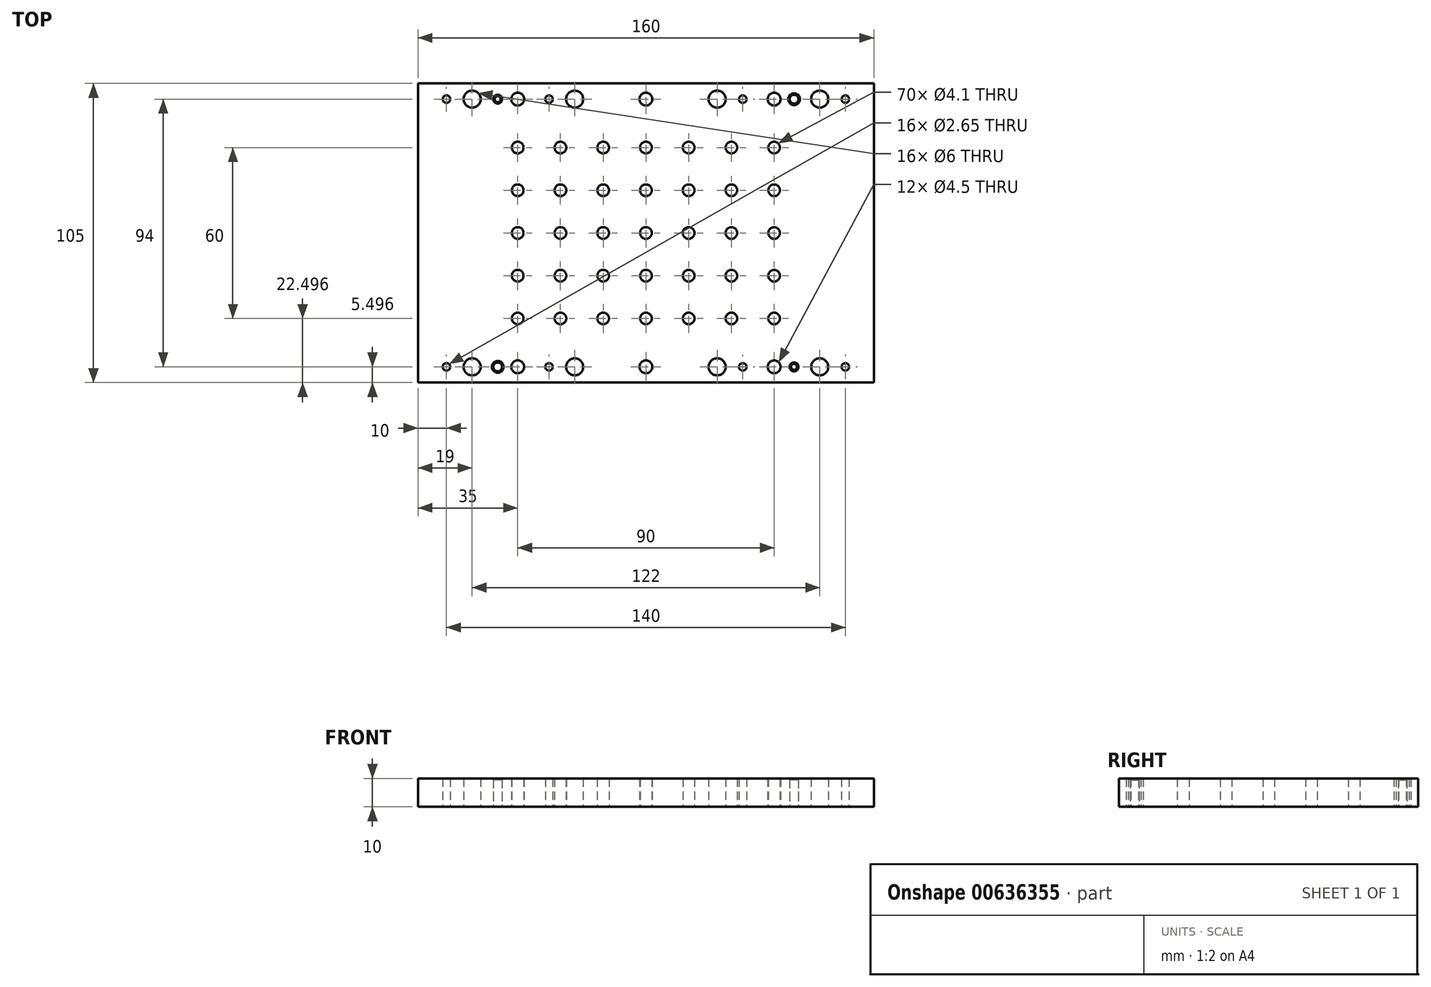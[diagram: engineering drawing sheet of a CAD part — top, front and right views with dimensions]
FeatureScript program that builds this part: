
annotation { "Feature Type Name" : "Feature", "Feature Type Description" : "" }
export const myFeature = defineFeature(function(context is Context, id is Id, definition is map)
    precondition{}
    {
        {
            var Q0;
            Q0=qCreatedBy(makeId("Top.planeOp"),FACE);
            var sketch = newSketch(context, id + "F0", { "sketchPlane" : qUnion([Q0])});
            skLineSegment(sketch, "E0.bottom", {"start": v(-90.54, 47.28) * mm, "end": v(69.46, 47.28) * mm});
            skLineSegment(sketch, "E0.top", {"start": v(-90.54, -57.72) * mm, "end": v(69.46, -57.72) * mm});
            skLineSegment(sketch, "E0.right", {"start": v(69.46, 47.28) * mm, "end": v(69.46, -57.72) * mm});
            skLineSegment(sketch, "E1", {"start": v(-90.54, -5.22) * mm, "end": v(69.46, -5.22) * mm, "construction": true});
            skCircle(sketch, "E2", {"center": v(-80.54, 41.78) * mm, "radius": 1.32 * mm});
            skCircle(sketch, "E3", {"center": v(-62.54, 41.78) * mm, "radius": 1.55 * mm});
            skCircle(sketch, "E4", {"center": v(-71.54, 41.78) * mm, "radius": 3 * mm});
            skCircle(sketch, "E5", {"center": v(-55.54, 41.78) * mm, "radius": 2.25 * mm});
            skCircle(sketch, "E6", {"center": v(-10.54, 41.78) * mm, "radius": 2.25 * mm});
            skCircle(sketch, "E7", {"center": v(-44.54, 41.78) * mm, "radius": 1.32 * mm});
            skCircle(sketch, "E8", {"center": v(-35.54, 41.78) * mm, "radius": 3 * mm});
            skCircle(sketch, "E9.MirrorC", {"center": v(50.46, 41.78) * mm, "radius": 3 * mm});
            skCircle(sketch, "E10.MirrorC", {"center": v(34.46, 41.78) * mm, "radius": 2.25 * mm});
            skCircle(sketch, "E11.MirrorC", {"center": v(14.46, 41.78) * mm, "radius": 3 * mm});
            skCircle(sketch, "E12.MirrorC", {"center": v(59.46, 41.78) * mm, "radius": 1.32 * mm});
            skCircle(sketch, "E13.MirrorC", {"center": v(41.46, 41.78) * mm, "radius": 1.55 * mm});
            skCircle(sketch, "E14.MirrorC", {"center": v(23.46, 41.78) * mm, "radius": 1.32 * mm});
            skCircle(sketch, "E15.MirrorC", {"center": v(59.46, -52.22) * mm, "radius": 1.32 * mm});
            skCircle(sketch, "E16.MirrorC", {"center": v(50.46, -52.22) * mm, "radius": 3 * mm});
            skCircle(sketch, "E17.MirrorC", {"center": v(41.46, -52.22) * mm, "radius": 1.55 * mm});
            skCircle(sketch, "E18.MirrorC", {"center": v(34.46, -52.22) * mm, "radius": 2.25 * mm});
            skCircle(sketch, "E19.MirrorC", {"center": v(23.46, -52.22) * mm, "radius": 1.32 * mm});
            skCircle(sketch, "E20.MirrorC", {"center": v(14.46, -52.22) * mm, "radius": 3 * mm});
            skCircle(sketch, "E21.MirrorC", {"center": v(-10.54, -52.22) * mm, "radius": 2.25 * mm});
            skCircle(sketch, "E22.MirrorC", {"center": v(-35.54, -52.22) * mm, "radius": 3 * mm});
            skCircle(sketch, "E23.MirrorC", {"center": v(-44.54, -52.22) * mm, "radius": 1.32 * mm});
            skCircle(sketch, "E24.MirrorC", {"center": v(-55.54, -52.22) * mm, "radius": 2.25 * mm});
            skCircle(sketch, "E25.MirrorC", {"center": v(-62.54, -52.22) * mm, "radius": 1.55 * mm});
            skCircle(sketch, "E26.MirrorC", {"center": v(-71.54, -52.22) * mm, "radius": 3 * mm});
            skCircle(sketch, "E27.MirrorC", {"center": v(-80.54, -52.22) * mm, "radius": 1.32 * mm});
            skLineSegment(sketch, "E28", {"start": v(-90.54, 47.28) * mm, "end": v(-90.54, -57.72) * mm});
            skCircle(sketch, "E29", {"center": v(-55.54, -35.22) * mm, "radius": 2.05 * mm});
            skCircle(sketch, "E30.0.1.0", {"center": v(-55.54, -20.22) * mm, "radius": 2.05 * mm});
            skCircle(sketch, "E30.0.2.0", {"center": v(-55.54, -5.22) * mm, "radius": 2.05 * mm});
            skCircle(sketch, "E30.0.3.0", {"center": v(-55.54, 9.78) * mm, "radius": 2.05 * mm});
            skCircle(sketch, "E30.0.4.0", {"center": v(-55.54, 24.78) * mm, "radius": 2.05 * mm});
            skCircle(sketch, "E30.1.0.0", {"center": v(-40.54, -35.22) * mm, "radius": 2.05 * mm});
            skCircle(sketch, "E30.1.1.0", {"center": v(-40.54, -20.22) * mm, "radius": 2.05 * mm});
            skCircle(sketch, "E30.1.2.0", {"center": v(-40.54, -5.22) * mm, "radius": 2.05 * mm});
            skCircle(sketch, "E30.1.3.0", {"center": v(-40.54, 9.78) * mm, "radius": 2.05 * mm});
            skCircle(sketch, "E30.1.4.0", {"center": v(-40.54, 24.78) * mm, "radius": 2.05 * mm});
            skCircle(sketch, "E30.2.0.0", {"center": v(-25.54, -35.22) * mm, "radius": 2.05 * mm});
            skCircle(sketch, "E30.2.1.0", {"center": v(-25.54, -20.22) * mm, "radius": 2.05 * mm});
            skCircle(sketch, "E30.2.2.0", {"center": v(-25.54, -5.22) * mm, "radius": 2.05 * mm});
            skCircle(sketch, "E30.2.3.0", {"center": v(-25.54, 9.78) * mm, "radius": 2.05 * mm});
            skCircle(sketch, "E30.2.4.0", {"center": v(-25.54, 24.78) * mm, "radius": 2.05 * mm});
            skCircle(sketch, "E30.3.0.0", {"center": v(-10.54, -35.22) * mm, "radius": 2.05 * mm});
            skCircle(sketch, "E30.3.1.0", {"center": v(-10.54, -20.22) * mm, "radius": 2.05 * mm});
            skCircle(sketch, "E30.3.2.0", {"center": v(-10.54, -5.22) * mm, "radius": 2.05 * mm});
            skCircle(sketch, "E30.3.3.0", {"center": v(-10.54, 9.78) * mm, "radius": 2.05 * mm});
            skCircle(sketch, "E30.3.4.0", {"center": v(-10.54, 24.78) * mm, "radius": 2.05 * mm});
            skCircle(sketch, "E30.4.0.0", {"center": v(4.46, -35.22) * mm, "radius": 2.05 * mm});
            skCircle(sketch, "E30.4.1.0", {"center": v(4.46, -20.22) * mm, "radius": 2.05 * mm});
            skCircle(sketch, "E30.4.2.0", {"center": v(4.46, -5.22) * mm, "radius": 2.05 * mm});
            skCircle(sketch, "E30.4.3.0", {"center": v(4.46, 9.78) * mm, "radius": 2.05 * mm});
            skCircle(sketch, "E30.4.4.0", {"center": v(4.46, 24.78) * mm, "radius": 2.05 * mm});
            skCircle(sketch, "E30.5.0.0", {"center": v(19.46, -35.22) * mm, "radius": 2.05 * mm});
            skCircle(sketch, "E30.5.1.0", {"center": v(19.46, -20.22) * mm, "radius": 2.05 * mm});
            skCircle(sketch, "E30.5.2.0", {"center": v(19.46, -5.22) * mm, "radius": 2.05 * mm});
            skCircle(sketch, "E30.5.3.0", {"center": v(19.46, 9.78) * mm, "radius": 2.05 * mm});
            skCircle(sketch, "E30.5.4.0", {"center": v(19.46, 24.78) * mm, "radius": 2.05 * mm});
            skCircle(sketch, "E30.6.0.0", {"center": v(34.46, -35.22) * mm, "radius": 2.05 * mm});
            skCircle(sketch, "E30.6.1.0", {"center": v(34.46, -20.22) * mm, "radius": 2.05 * mm});
            skCircle(sketch, "E30.6.2.0", {"center": v(34.46, -5.22) * mm, "radius": 2.05 * mm});
            skCircle(sketch, "E30.6.3.0", {"center": v(34.46, 9.78) * mm, "radius": 2.05 * mm});
            skCircle(sketch, "E30.6.4.0", {"center": v(34.46, 24.78) * mm, "radius": 2.05 * mm});
            skSolve(sketch);
        }
        {
            var Q0;
            Q0=sQuery(id+"F0.wireOp",EDGE,"E28");
            var Q1;
            Q1=sQuery(id+"F0.wireOp",EDGE,"E0.bottom");
            var Q2;
            Q2=sQuery(id+"F0.wireOp",EDGE,"E0.top");
            var Q3;
            Q3=sQuery(id+"F0.wireOp",EDGE,"E0.right");
            extrude(context, id + "F1", {"bodyType" : ToolBodyType.SURFACE, "surfaceEntities" : qUnion([Q0, Q1, Q2, Q3]), "oppositeDirection" : true, "depth" : 5 * mm, "offsetDistance" : 25 * mm});
        }
        {
            var Q0;
            Q0=sQuery(id+"F0.wireOp",EDGE,"E30.0.4.0");
            var Q1;
            Q1=sQuery(id+"F0.wireOp",EDGE,"E30.0.3.0");
            var Q2;
            Q2=sQuery(id+"F0.wireOp",EDGE,"E30.0.2.0");
            var Q3;
            Q3=sQuery(id+"F0.wireOp",EDGE,"E30.0.1.0");
            var Q4;
            Q4=sQuery(id+"F0.wireOp",EDGE,"E29");
            var Q5;
            Q5=sQuery(id+"F0.wireOp",EDGE,"E30.1.0.0");
            var Q6;
            Q6=sQuery(id+"F0.wireOp",EDGE,"E30.2.0.0");
            var Q7;
            Q7=sQuery(id+"F0.wireOp",EDGE,"E30.2.1.0");
            var Q8;
            Q8=sQuery(id+"F0.wireOp",EDGE,"E30.1.1.0");
            var Q9;
            Q9=sQuery(id+"F0.wireOp",EDGE,"E30.1.2.0");
            var Q10;
            Q10=sQuery(id+"F0.wireOp",EDGE,"E30.2.2.0");
            var Q11;
            Q11=sQuery(id+"F0.wireOp",EDGE,"E30.1.3.0");
            var Q12;
            Q12=sQuery(id+"F0.wireOp",EDGE,"E30.2.3.0");
            var Q13;
            Q13=sQuery(id+"F0.wireOp",EDGE,"E30.2.4.0");
            var Q14;
            Q14=sQuery(id+"F0.wireOp",EDGE,"E30.1.4.0");
            var Q15;
            Q15=sQuery(id+"F0.wireOp",EDGE,"E30.3.4.0");
            var Q16;
            Q16=sQuery(id+"F0.wireOp",EDGE,"E30.3.3.0");
            var Q17;
            Q17=sQuery(id+"F0.wireOp",EDGE,"E30.3.2.0");
            var Q18;
            Q18=sQuery(id+"F0.wireOp",EDGE,"E30.3.1.0");
            var Q19;
            Q19=sQuery(id+"F0.wireOp",EDGE,"E30.3.0.0");
            var Q20;
            Q20=sQuery(id+"F0.wireOp",EDGE,"E30.4.0.0");
            var Q21;
            Q21=sQuery(id+"F0.wireOp",EDGE,"E30.4.1.0");
            var Q22;
            Q22=sQuery(id+"F0.wireOp",EDGE,"E30.4.2.0");
            var Q23;
            Q23=sQuery(id+"F0.wireOp",EDGE,"E30.4.3.0");
            var Q24;
            Q24=sQuery(id+"F0.wireOp",EDGE,"E30.4.4.0");
            var Q25;
            Q25=sQuery(id+"F0.wireOp",EDGE,"E30.5.4.0");
            var Q26;
            Q26=sQuery(id+"F0.wireOp",EDGE,"E30.5.3.0");
            var Q27;
            Q27=sQuery(id+"F0.wireOp",EDGE,"E30.5.2.0");
            var Q28;
            Q28=sQuery(id+"F0.wireOp",EDGE,"E30.5.1.0");
            var Q29;
            Q29=sQuery(id+"F0.wireOp",EDGE,"E30.5.0.0");
            var Q30;
            Q30=sQuery(id+"F0.wireOp",EDGE,"E30.6.0.0");
            var Q31;
            Q31=sQuery(id+"F0.wireOp",EDGE,"E30.6.1.0");
            var Q32;
            Q32=sQuery(id+"F0.wireOp",EDGE,"E30.6.2.0");
            var Q33;
            Q33=sQuery(id+"F0.wireOp",EDGE,"E30.6.3.0");
            var Q34;
            Q34=sQuery(id+"F0.wireOp",EDGE,"E30.6.4.0");
            extrude(context, id + "F2", {"bodyType" : ToolBodyType.SURFACE, "surfaceEntities" : qUnion([Q0, Q1, Q2, Q3, Q4, Q5, Q6, Q7, Q8, Q9, Q10, Q11, Q12, Q13, Q14, Q15, Q16, Q17, Q18, Q19, Q20, Q21, Q22, Q23, Q24, Q25, Q26, Q27, Q28, Q29, Q30, Q31, Q32, Q33, Q34]), "oppositeDirection" : true, "depth" : 0.4 * mm, "offsetDistance" : 25 * mm});
        }
        {
            var Q0;
            Q0=sQuery(id+"F0.wireOp",EDGE,"E2");
            var Q1;
            Q1=sQuery(id+"F0.wireOp",EDGE,"E4");
            var Q2;
            Q2=sQuery(id+"F0.wireOp",EDGE,"E5");
            var Q3;
            Q3=sQuery(id+"F0.wireOp",EDGE,"E7");
            var Q4;
            Q4=sQuery(id+"F0.wireOp",EDGE,"E8");
            var Q5;
            Q5=sQuery(id+"F0.wireOp",EDGE,"E6");
            var Q6;
            Q6=sQuery(id+"F0.wireOp",EDGE,"E11.MirrorC");
            var Q7;
            Q7=sQuery(id+"F0.wireOp",EDGE,"E14.MirrorC");
            var Q8;
            Q8=sQuery(id+"F0.wireOp",EDGE,"E12.MirrorC");
            var Q9;
            Q9=sQuery(id+"F0.wireOp",EDGE,"E9.MirrorC");
            var Q10;
            Q10=sQuery(id+"F0.wireOp",EDGE,"E10.MirrorC");
            extrude(context, id + "F3", {"bodyType" : ToolBodyType.SURFACE, "surfaceEntities" : qUnion([Q0, Q1, Q2, Q3, Q4, Q5, Q6, Q7, Q8, Q9, Q10]), "oppositeDirection" : true, "depth" : 5 * mm, "offsetDistance" : 25 * mm});
        }
        {
            var Q0;
            Q0=sQuery(id+"F0.wireOp",EDGE,"E27.MirrorC");
            var Q1;
            Q1=sQuery(id+"F0.wireOp",EDGE,"E26.MirrorC");
            var Q2;
            Q2=sQuery(id+"F0.wireOp",EDGE,"E24.MirrorC");
            var Q3;
            Q3=sQuery(id+"F0.wireOp",EDGE,"E23.MirrorC");
            var Q4;
            Q4=sQuery(id+"F0.wireOp",EDGE,"E22.MirrorC");
            var Q5;
            Q5=sQuery(id+"F0.wireOp",EDGE,"E21.MirrorC");
            var Q6;
            Q6=sQuery(id+"F0.wireOp",EDGE,"E20.MirrorC");
            var Q7;
            Q7=sQuery(id+"F0.wireOp",EDGE,"E19.MirrorC");
            var Q8;
            Q8=sQuery(id+"F0.wireOp",EDGE,"E18.MirrorC");
            var Q9;
            Q9=sQuery(id+"F0.wireOp",EDGE,"E16.MirrorC");
            var Q10;
            Q10=sQuery(id+"F0.wireOp",EDGE,"E15.MirrorC");
            extrude(context, id + "F4", {"bodyType" : ToolBodyType.SURFACE, "surfaceEntities" : qUnion([Q0, Q1, Q2, Q3, Q4, Q5, Q6, Q7, Q8, Q9, Q10]), "oppositeDirection" : true, "depth" : 5 * mm, "offsetDistance" : 25 * mm});
        }
        {
            var Q0;
            Q0=makeQuery(id+"F0.imprint","IMPRINT",FACE,{"disambiguationData":[TD([[makeQuery(id+"F0.imprint","IMPRINT",EDGE,{"derivedFrom":sQuery(id+"F0.wireOp",EDGE,"E25.MirrorC")}),-1.0]])]});
            var Q1;
            Q1=sQuery(id+"F0.wireOp",EDGE,"E25.MirrorC");
            extrude(context, id + "F5", {"entities" : qUnion([Q0]), "surfaceEntities" : qUnion([Q1]), "endBound" : BoundingType.SYMMETRIC, "depth" : 10 * mm, "offsetDistance" : 25 * mm});
        }
        {
            var Q0;
            Q0=makeQuery(id+"F5.opExtrude","CAP_EDGE",EDGE,{"disambiguationData":[OSD([sQuery(id+"F0.wireOp",EDGE,"E25.MirrorC")])],"isStart":false});
            chamfer(context, id + "F6", {"entities" : qUnion([Q0]), "width" : 0.5 * mm, "tangentPropagation" : true});
        }
        {
            var Q0;
            Q0=makeQuery(id+"F0.imprint","IMPRINT",FACE,{"disambiguationData":[TD([[makeQuery(id+"F0.imprint","IMPRINT",EDGE,{"derivedFrom":sQuery(id+"F0.wireOp",EDGE,"E17.MirrorC")}),1.0]])]});
            var Q1;
            Q1=sQuery(id+"F0.wireOp",EDGE,"E17.MirrorC");
            extrude(context, id + "F7", {"entities" : qUnion([Q0]), "surfaceEntities" : qUnion([Q1]), "endBound" : BoundingType.SYMMETRIC, "depth" : 10 * mm, "offsetDistance" : 25 * mm});
        }
        {
            var Q0;
            Q0=makeQuery(id+"F7.opExtrude","CAP_EDGE",EDGE,{"disambiguationData":[OSD([sQuery(id+"F0.wireOp",EDGE,"E17.MirrorC")])],"isStart":false});
            chamfer(context, id + "F8", {"entities" : qUnion([Q0]), "width" : 0.5 * mm, "tangentPropagation" : true});
        }
        {
            var Q0;
            Q0=makeQuery(id+"F0.imprint","IMPRINT",FACE,{"disambiguationData":[TD([[makeQuery(id+"F0.imprint","IMPRINT",EDGE,{"derivedFrom":sQuery(id+"F0.wireOp",EDGE,"E13.MirrorC")}),-1.0]])]});
            var Q1;
            Q1=sQuery(id+"F0.wireOp",EDGE,"E13.MirrorC");
            extrude(context, id + "F9", {"entities" : qUnion([Q0]), "surfaceEntities" : qUnion([Q1]), "endBound" : BoundingType.SYMMETRIC, "depth" : 10 * mm, "offsetDistance" : 25 * mm});
        }
        {
            var Q0;
            Q0=makeQuery(id+"F9.opExtrude","CAP_EDGE",EDGE,{"disambiguationData":[OSD([sQuery(id+"F0.wireOp",EDGE,"E13.MirrorC")])],"isStart":false});
            chamfer(context, id + "F10", {"entities" : qUnion([Q0]), "width" : 0.5 * mm, "tangentPropagation" : true});
        }
        {
            var Q0;
            Q0=makeQuery(id+"F0.imprint","IMPRINT",FACE,{"disambiguationData":[TD([[makeQuery(id+"F0.imprint","IMPRINT",EDGE,{"derivedFrom":sQuery(id+"F0.wireOp",EDGE,"E3")}),1.0]])]});
            var Q1;
            Q1=sQuery(id+"F0.wireOp",EDGE,"E3");
            extrude(context, id + "F11", {"entities" : qUnion([Q0]), "surfaceEntities" : qUnion([Q1]), "endBound" : BoundingType.SYMMETRIC, "depth" : 10 * mm, "offsetDistance" : 25 * mm});
        }
        {
            var Q0;
            Q0=makeQuery(id+"F11.opExtrude","CAP_EDGE",EDGE,{"disambiguationData":[OSD([sQuery(id+"F0.wireOp",EDGE,"E3")])],"isStart":false});
            chamfer(context, id + "F12", {"entities" : qUnion([Q0]), "width" : 0.5 * mm});
        }
    });
